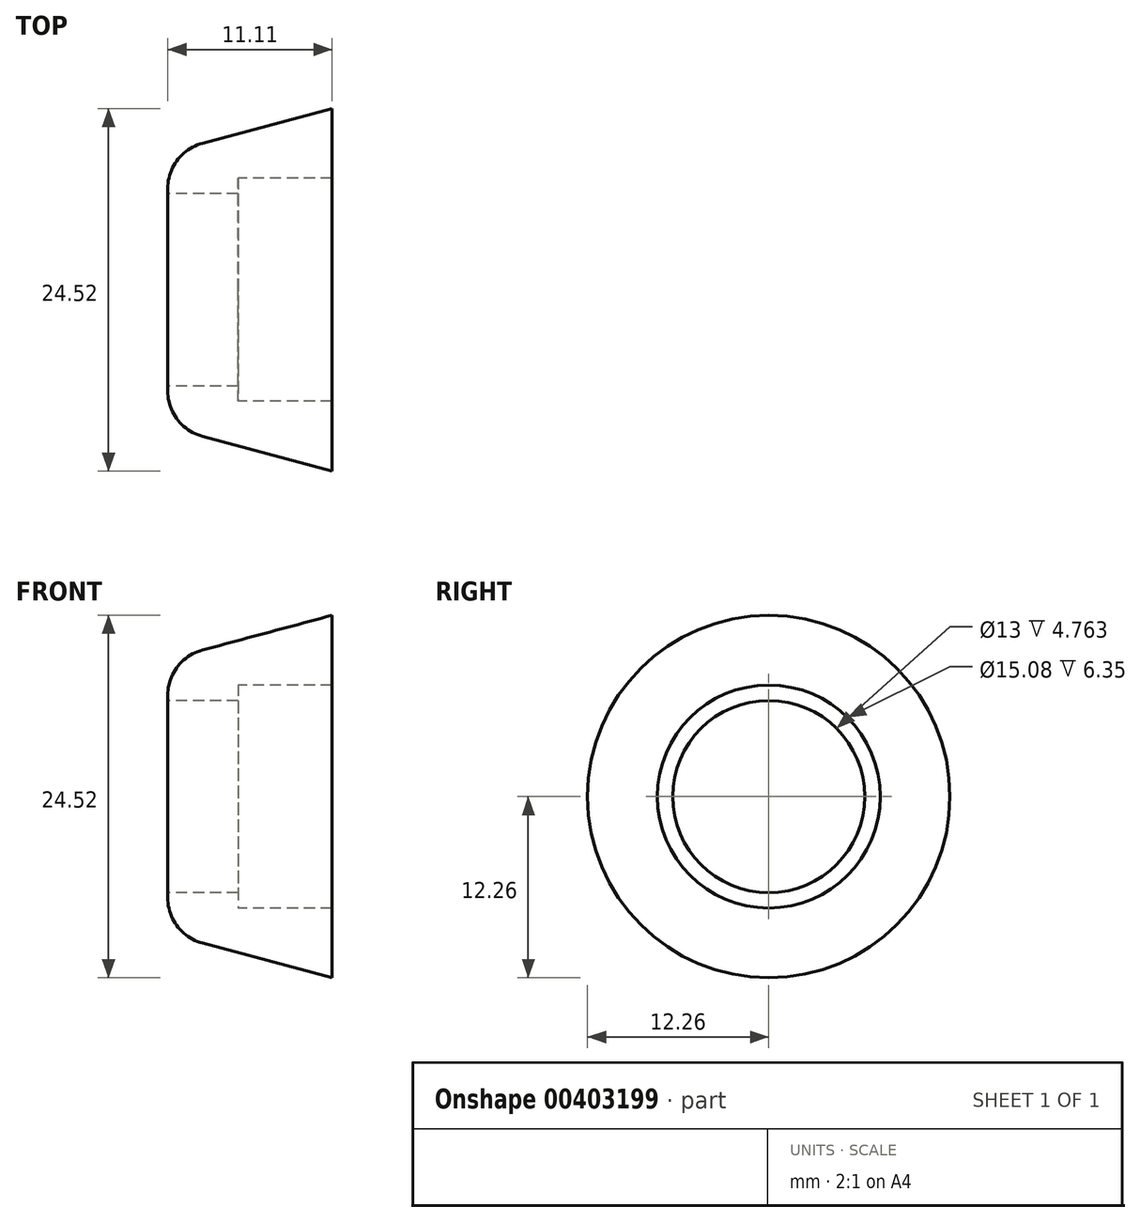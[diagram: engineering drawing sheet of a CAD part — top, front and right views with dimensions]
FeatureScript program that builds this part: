
annotation { "Feature Type Name" : "Feature", "Feature Type Description" : "" }
export const myFeature = defineFeature(function(context is Context, id is Id, definition is map)
    precondition{}
    {
        {
            var Q0;
            Q0=qCreatedBy(makeId("Front.planeOp"),FACE);
            var sketch = newSketch(context, id + "F0", { "sketchPlane" : qUnion([Q0])});
            skLineSegment(sketch, "E0", {"start": v(0, 12.26) * mm, "end": v(-8.76, 9.9) * mm});
            skLineSegment(sketch, "E1", {"start": v(-11.11, 6.84) * mm, "end": v(-11.11, 6.5) * mm});
            skPoint(sketch, "E2.visualSharp", {"position": v(-11.11, 9.28) * mm});
            skArc(sketch, "E2.filletArc", {"start": v(-8.76, 9.9) * mm, "mid": v(-10.46, 8.77) * mm, "end": v(-11.11, 6.84) * mm});
            skLineSegment(sketch, "E3", {"start": v(0, 12.26) * mm, "end": v(0, 7.54) * mm});
            skLineSegment(sketch, "E4", {"start": v(-79.3, 0) * mm, "end": v(89.8, 0) * mm, "construction": true});
            skLineSegment(sketch, "E5", {"start": v(-11.11, 6.5) * mm, "end": v(-6.35, 6.5) * mm});
            skLineSegment(sketch, "E6", {"start": v(-6.35, 6.5) * mm, "end": v(-6.35, 7.54) * mm});
            skLineSegment(sketch, "E7", {"start": v(-6.35, 7.54) * mm, "end": v(0, 7.54) * mm});
            skSolve(sketch);
        }
        {
            var Q0;
            Q0=makeQuery(id+"F0.imprint","IMPRINT",FACE,{"disambiguationData":[TD([[makeQuery(id+"F0.imprint","IMPRINT",EDGE,{"derivedFrom":sQuery(id+"F0.wireOp",EDGE,"iFIy6t9p-DLf4-Kr0U-XxBy-TVTDalWC6sph")}),1.0]])]});
            var Q1;
            Q1=makeQuery(id+"F0.imprint","IMPRINT",FACE,{"disambiguationData":[TD([[makeQuery(id+"F0.imprint","IMPRINT",EDGE,{"derivedFrom":sQuery(id+"F0.wireOp",EDGE,"E0")}),1.0]])]});
            var Q2;
            Q2=sQuery(id+"F0.wireOp",EDGE,"E4");
            revolve(context, id + "F1", {"entities" : qUnion([Q0, Q1]), "axis" : qUnion([Q2]), "revolveType" : RevolveType.FULL});
        }
    });
